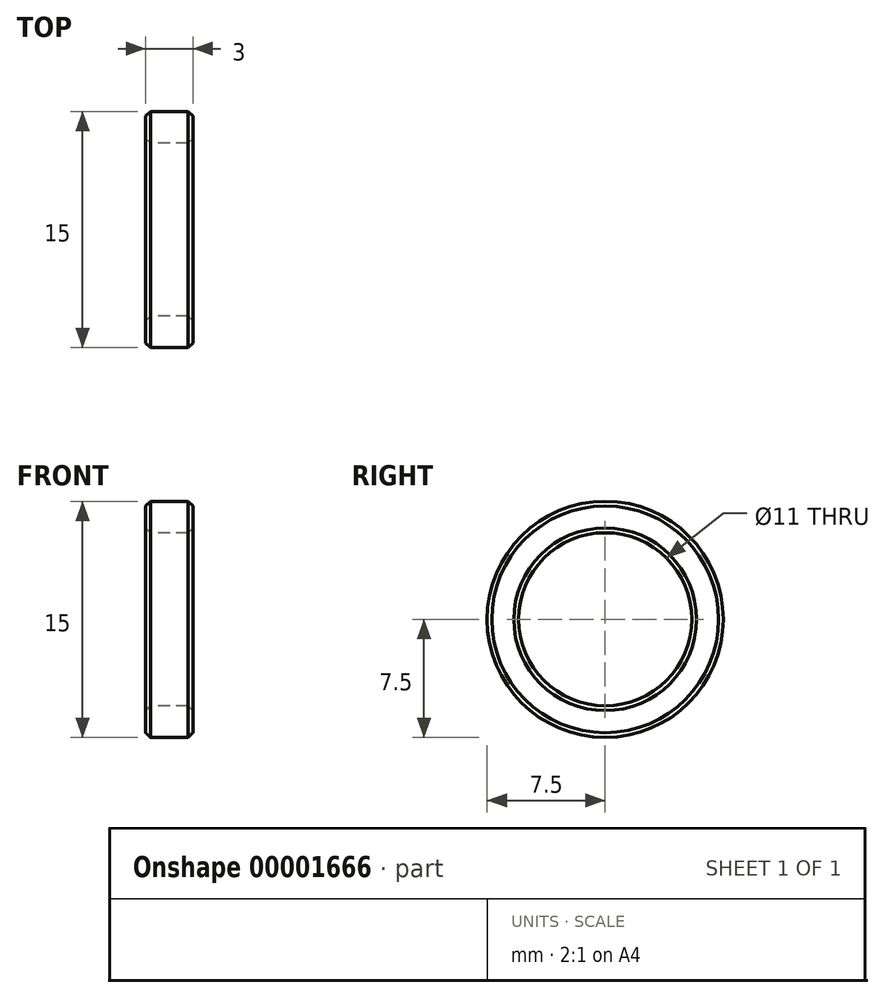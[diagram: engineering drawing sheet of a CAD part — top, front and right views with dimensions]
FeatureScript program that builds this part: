
annotation { "Feature Type Name" : "Feature", "Feature Type Description" : "" }
export const myFeature = defineFeature(function(context is Context, id is Id, definition is map)
    precondition{}
    {
        {
            var Q0;
            Q0=qCreatedBy(makeId("Right.planeOp"),FACE);
            var sketch = newSketch(context, id + "F0", { "sketchPlane" : qUnion([Q0])});
            skCircle(sketch, "E0", {"center": v(0, 0) * mm, "radius": 5.5 * mm});
            skCircle(sketch, "E1", {"center": v(0, 0) * mm, "radius": 7.5 * mm});
            skSolve(sketch);
        }
        {
            var Q0;
            Q0=makeQuery(id+"F0.imprint","IMPRINT",FACE,{"disambiguationData":[TD([[makeQuery(id+"F0.imprint","IMPRINT",EDGE,{"derivedFrom":sQuery(id+"F0.wireOp",EDGE,"E0")}),-1.0]])]});
            extrude(context, id + "F1", {"entities" : qUnion([Q0]), "endBound" : BoundingType.SYMMETRIC, "depth" : 3 * mm});
        }
        {
            var Q0;
            Q0=makeQuery(id+"F1.opExtrude","SWEPT_FACE",FACE,{"disambiguationData":[OSD([sQuery(id+"F0.wireOp",EDGE,"E1")])]});
            var Q1;
            Q1=makeQuery(id+"F1.opExtrude","SWEPT_FACE",FACE,{"disambiguationData":[OSD([sQuery(id+"F0.wireOp",EDGE,"E0")])]});
            chamfer(context, id + "F2", {"entities" : qUnion([Q0, Q1]), "width" : .3 * mm, "tangentPropagation" : true});
        }
    });
